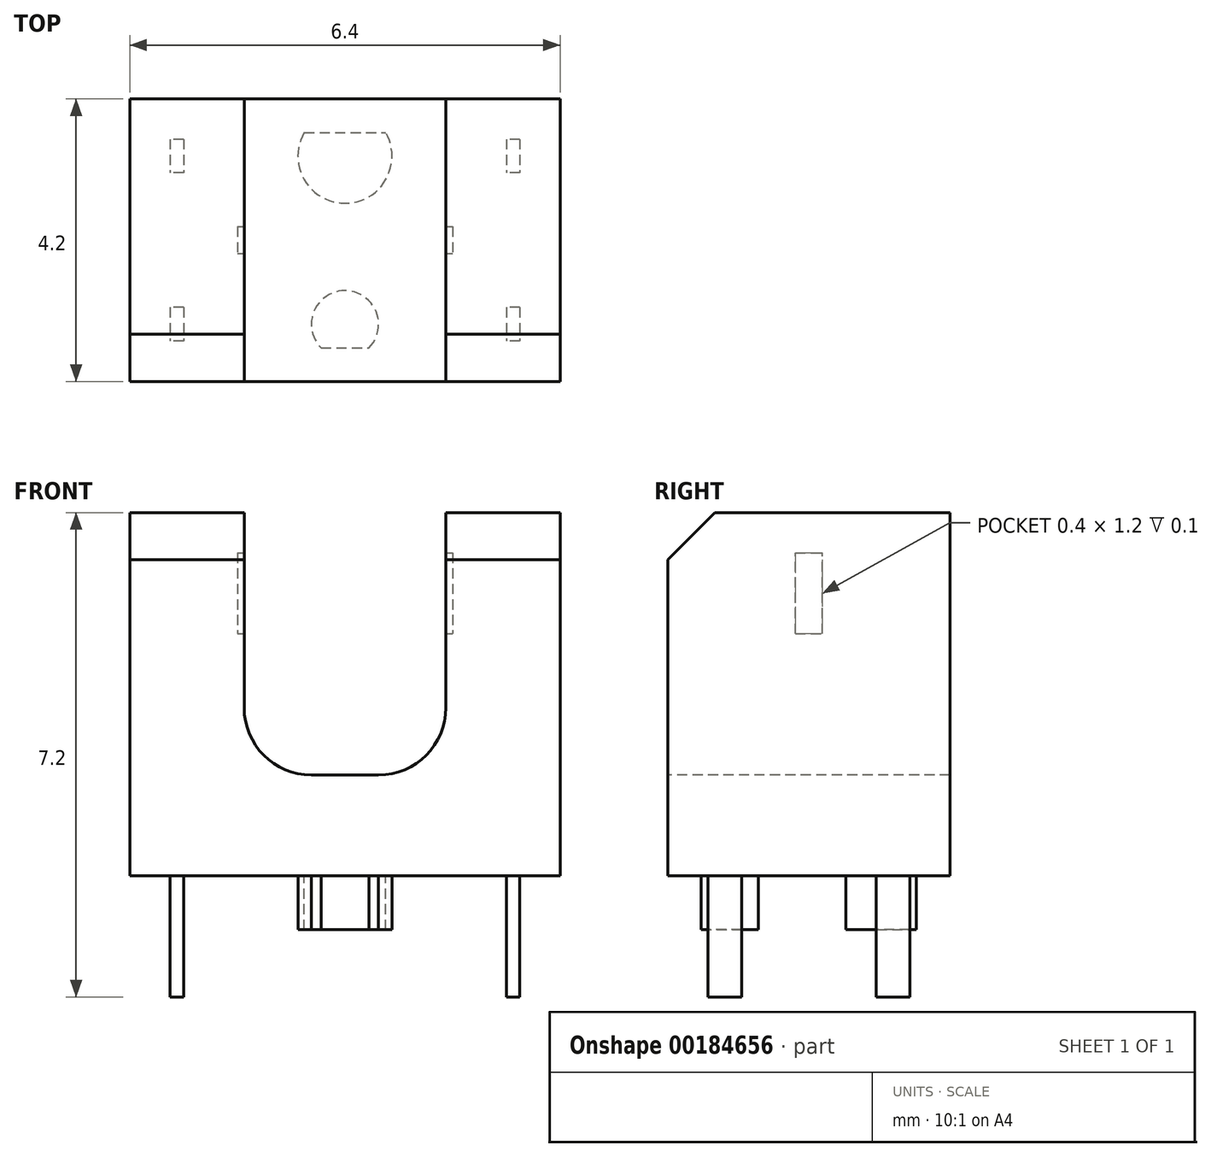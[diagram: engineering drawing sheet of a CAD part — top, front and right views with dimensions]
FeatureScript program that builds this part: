
annotation { "Feature Type Name" : "Feature", "Feature Type Description" : "" }
export const myFeature = defineFeature(function(context is Context, id is Id, definition is map)
    precondition{}
    {
        {
            var Q0;
            Q0=qCreatedBy(makeId("Top.planeOp"),FACE);
            var sketch = newSketch(context, id + "F0", { "sketchPlane" : qUnion([Q0])});
            skLineSegment(sketch, "E0.rect.bottom", {"start": v(3.2, 2.1) * mm, "end": v(-3.2, 2.1) * mm});
            skLineSegment(sketch, "E0.rect.top", {"start": v(3.2, -2.1) * mm, "end": v(-3.2, -2.1) * mm});
            skLineSegment(sketch, "E0.rect.left", {"start": v(3.2, 2.1) * mm, "end": v(3.2, -2.1) * mm});
            skLineSegment(sketch, "E0.rect.right", {"start": v(-3.2, 2.1) * mm, "end": v(-3.2, -2.1) * mm});
            skPoint(sketch, "E0.rect.middle", {"position": v(0, 0) * mm});
            skSolve(sketch);
        }
        {
            var Q0;
            Q0=qSketchRegion(id+"F0",true);
            extrude(context, id + "F1", {"entities" : qUnion([Q0]), "depth" : 5.4 * mm});
        }
        {
            var Q0;
            Q0=makeQuery(id+"F1.opExtrude","SWEPT_FACE",FACE,{"disambiguationData":[OSD([sQuery(id+"F0.wireOp",EDGE,"E0.rect.top")])]});
            var sketch = newSketch(context, id + "F2", { "sketchPlane" : qUnion([Q0])});
            skLineSegment(sketch, "E1.rect.bottom", {"start": v(1.5, 5.4) * mm, "end": v(-1.5, 5.4) * mm});
            skLineSegment(sketch, "E1.rect.top", {"start": v(0.5, 1.5) * mm, "end": v(-0.5, 1.5) * mm});
            skLineSegment(sketch, "E1.rect.left", {"start": v(1.5, 5.4) * mm, "end": v(1.5, 2.5) * mm});
            skLineSegment(sketch, "E1.rect.right", {"start": v(-1.5, 5.4) * mm, "end": v(-1.5, 2.5) * mm});
            skPoint(sketch, "E1.rect.middle", {"position": v(0, 3.45) * mm});
            skPoint(sketch, "E2.visualSharp", {"position": v(-1.5, 1.5) * mm});
            skArc(sketch, "E2.filletArc", {"start": v(-1.5, 2.5) * mm, "mid": v(-1.2, 1.8) * mm, "end": v(-0.5, 1.5) * mm});
            skPoint(sketch, "E3.visualSharp", {"position": v(1.5, 1.5) * mm});
            skArc(sketch, "E3.filletArc", {"start": v(0.5, 1.5) * mm, "mid": v(1.2, 1.8) * mm, "end": v(1.5, 2.5) * mm});
            skSolve(sketch);
        }
        {
            var Q0;
            Q0=qSketchRegion(id+"F2",true);
            var Q1;
            Q1=makeQuery(id+"F1.opExtrude","SWEPT_FACE",FACE,{"disambiguationData":[OSD([sQuery(id+"F0.wireOp",EDGE,"E0.rect.bottom")])]});
            extrude(context, id + "F3", {"entities" : qUnion([Q0]), "operationType" : NewBodyOperationType.REMOVE, "endBound" : BoundingType.UP_TO_SURFACE, "oppositeDirection" : true, "endBoundEntityFace" : qUnion([Q1]), "depth" : 25 * mm});
        }
        {
            var Q0;
            {var subQ0=sQuery(id+"F0.wireOp",EDGE,"E0.rect.right");var subQ1=sQuery(id+"F0.wireOp",EDGE,"E0.rect.top");Q0=makeQuery(id+"F3.boolean.opBoolean","SPLIT",EDGE,{"disambiguationData":[TD([makeQuery(id+"F1.opExtrude","SWEPT_FACE",FACE,{"disambiguationData":[OSD([subQ0])]})])],"derivedFrom":makeQuery(id+"F1.opExtrude","CAP_EDGE",EDGE,{"disambiguationData":[OSD([subQ1])],"isStart":false})});}
            var Q1;
            {var subQ0=sQuery(id+"F0.wireOp",EDGE,"E0.rect.left");var subQ1=sQuery(id+"F0.wireOp",EDGE,"E0.rect.top");Q1=makeQuery(id+"F3.boolean.opBoolean","SPLIT",EDGE,{"disambiguationData":[TD([makeQuery(id+"F1.opExtrude","SWEPT_FACE",FACE,{"disambiguationData":[OSD([subQ0])]})])],"derivedFrom":makeQuery(id+"F1.opExtrude","CAP_EDGE",EDGE,{"disambiguationData":[OSD([subQ1])],"isStart":false})});}
            chamfer(context, id + "F4", {"entities" : qUnion([Q0, Q1]), "width" : 0.7 * mm, "tangentPropagation" : true});
        }
        {
            var Q0;
            Q0=qCreatedBy(makeId("Right.planeOp"),FACE);
            var sketch = newSketch(context, id + "F5", { "sketchPlane" : qUnion([Q0])});
            skLineSegment(sketch, "E4.rect.bottom", {"start": v(0.2, 4.8) * mm, "end": v(-0.2, 4.8) * mm});
            skLineSegment(sketch, "E4.rect.top", {"start": v(0.2, 3.6) * mm, "end": v(-0.2, 3.6) * mm});
            skLineSegment(sketch, "E4.rect.left", {"start": v(0.2, 4.8) * mm, "end": v(0.2, 3.6) * mm});
            skLineSegment(sketch, "E4.rect.right", {"start": v(-0.2, 4.8) * mm, "end": v(-0.2, 3.6) * mm});
            skPoint(sketch, "E4.rect.middle", {"position": v(0, 4.2) * mm});
            skSolve(sketch);
        }
        {
            var Q0;
            Q0=qSketchRegion(id+"F5",true);
            extrude(context, id + "F6", {"entities" : qUnion([Q0]), "operationType" : NewBodyOperationType.REMOVE, "endBound" : BoundingType.SYMMETRIC, "oppositeDirection" : true, "depth" : 3.2 * mm});
        }
        {
            var Q0;
            Q0=makeQuery(id+"F1.opExtrude","CAP_FACE",FACE,{"disambiguationData":[OSD([sQuery(id+"F0.wireOp",EDGE,"E0.rect.bottom"),sQuery(id+"F0.wireOp",EDGE,"E0.rect.top"),sQuery(id+"F0.wireOp",EDGE,"E0.rect.left"),sQuery(id+"F0.wireOp",EDGE,"E0.rect.right")])],"isStart":true});
            var sketch = newSketch(context, id + "F7", { "sketchPlane" : qUnion([Q0])});
            skArc(sketch, "E5", {"start": v(-0.36, 1.6) * mm, "mid": v(0, 0.75) * mm, "end": v(0.36, 1.6) * mm});
            skArc(sketch, "E6", {"start": v(0.6, -1.6) * mm, "mid": v(0, -0.55) * mm, "end": v(-0.6, -1.6) * mm});
            skLineSegment(sketch, "E7", {"start": v(-0.36, 1.6) * mm, "end": v(0.36, 1.6) * mm});
            skLineSegment(sketch, "E8", {"start": v(-0.6, -1.6) * mm, "end": v(0.6, -1.6) * mm});
            skSolve(sketch);
        }
        {
            var Q0;
            Q0=qSketchRegion(id+"F7",true);
            extrude(context, id + "F8", {"entities" : qUnion([Q0]), "operationType" : NewBodyOperationType.ADD, "depth" : 0.8 * mm});
        }
        {
            var Q0;
            Q0=makeQuery(id+"F1.opExtrude","CAP_FACE",FACE,{"disambiguationData":[OSD([sQuery(id+"F0.wireOp",EDGE,"E0.rect.bottom"),sQuery(id+"F0.wireOp",EDGE,"E0.rect.top"),sQuery(id+"F0.wireOp",EDGE,"E0.rect.left"),sQuery(id+"F0.wireOp",EDGE,"E0.rect.right")])],"isStart":true});
            var sketch = newSketch(context, id + "F9", { "sketchPlane" : qUnion([Q0])});
            skLineSegment(sketch, "E9.rect.bottom", {"start": v(-2.4, 1) * mm, "end": v(-2.6, 1) * mm});
            skLineSegment(sketch, "E9.rect.top", {"start": v(-2.4, 1.5) * mm, "end": v(-2.6, 1.5) * mm});
            skLineSegment(sketch, "E9.rect.left", {"start": v(-2.4, 1) * mm, "end": v(-2.4, 1.5) * mm});
            skLineSegment(sketch, "E9.rect.right", {"start": v(-2.6, 1) * mm, "end": v(-2.6, 1.5) * mm});
            skPoint(sketch, "E9.rect.middle", {"position": v(-2.5, 1.25) * mm});
            skLineSegment(sketch, "E10.0.1.0", {"start": v(-2.6, -1.5) * mm, "end": v(-2.6, -1) * mm});
            skLineSegment(sketch, "E10.0.1.1", {"start": v(-2.4, -1.5) * mm, "end": v(-2.6, -1.5) * mm});
            skLineSegment(sketch, "E10.0.1.2", {"start": v(-2.4, -1.5) * mm, "end": v(-2.4, -1) * mm});
            skLineSegment(sketch, "E10.0.1.3", {"start": v(-2.4, -1) * mm, "end": v(-2.6, -1) * mm});
            skPoint(sketch, "E10.0.1.4", {"position": v(-2.5, -1.25) * mm});
            skLineSegment(sketch, "E10.1.0.0", {"start": v(2.4, 1) * mm, "end": v(2.4, 1.5) * mm});
            skLineSegment(sketch, "E10.1.0.1", {"start": v(2.6, 1) * mm, "end": v(2.4, 1) * mm});
            skLineSegment(sketch, "E10.1.0.2", {"start": v(2.6, 1) * mm, "end": v(2.6, 1.5) * mm});
            skLineSegment(sketch, "E10.1.0.3", {"start": v(2.6, 1.5) * mm, "end": v(2.4, 1.5) * mm});
            skPoint(sketch, "E10.1.0.4", {"position": v(2.5, 1.25) * mm});
            skLineSegment(sketch, "E10.1.1.0", {"start": v(2.4, -1.5) * mm, "end": v(2.4, -1) * mm});
            skLineSegment(sketch, "E10.1.1.1", {"start": v(2.6, -1.5) * mm, "end": v(2.4, -1.5) * mm});
            skLineSegment(sketch, "E10.1.1.2", {"start": v(2.6, -1.5) * mm, "end": v(2.6, -1) * mm});
            skLineSegment(sketch, "E10.1.1.3", {"start": v(2.6, -1) * mm, "end": v(2.4, -1) * mm});
            skPoint(sketch, "E10.1.1.4", {"position": v(2.5, -1.25) * mm});
            skLineSegment(sketch, "E10.direction1", {"start": v(-2.6, 1) * mm, "end": v(2.4, 1) * mm, "construction": true});
            skLineSegment(sketch, "E10.direction2", {"start": v(-2.6, 1) * mm, "end": v(-2.6, -1.5) * mm, "construction": true});
            skSolve(sketch);
        }
        {
            var Q0;
            Q0=qSketchRegion(id+"F9",true);
            extrude(context, id + "F10", {"entities" : qUnion([Q0]), "operationType" : NewBodyOperationType.ADD, "depth" : 1.8 * mm});
        }
    });
